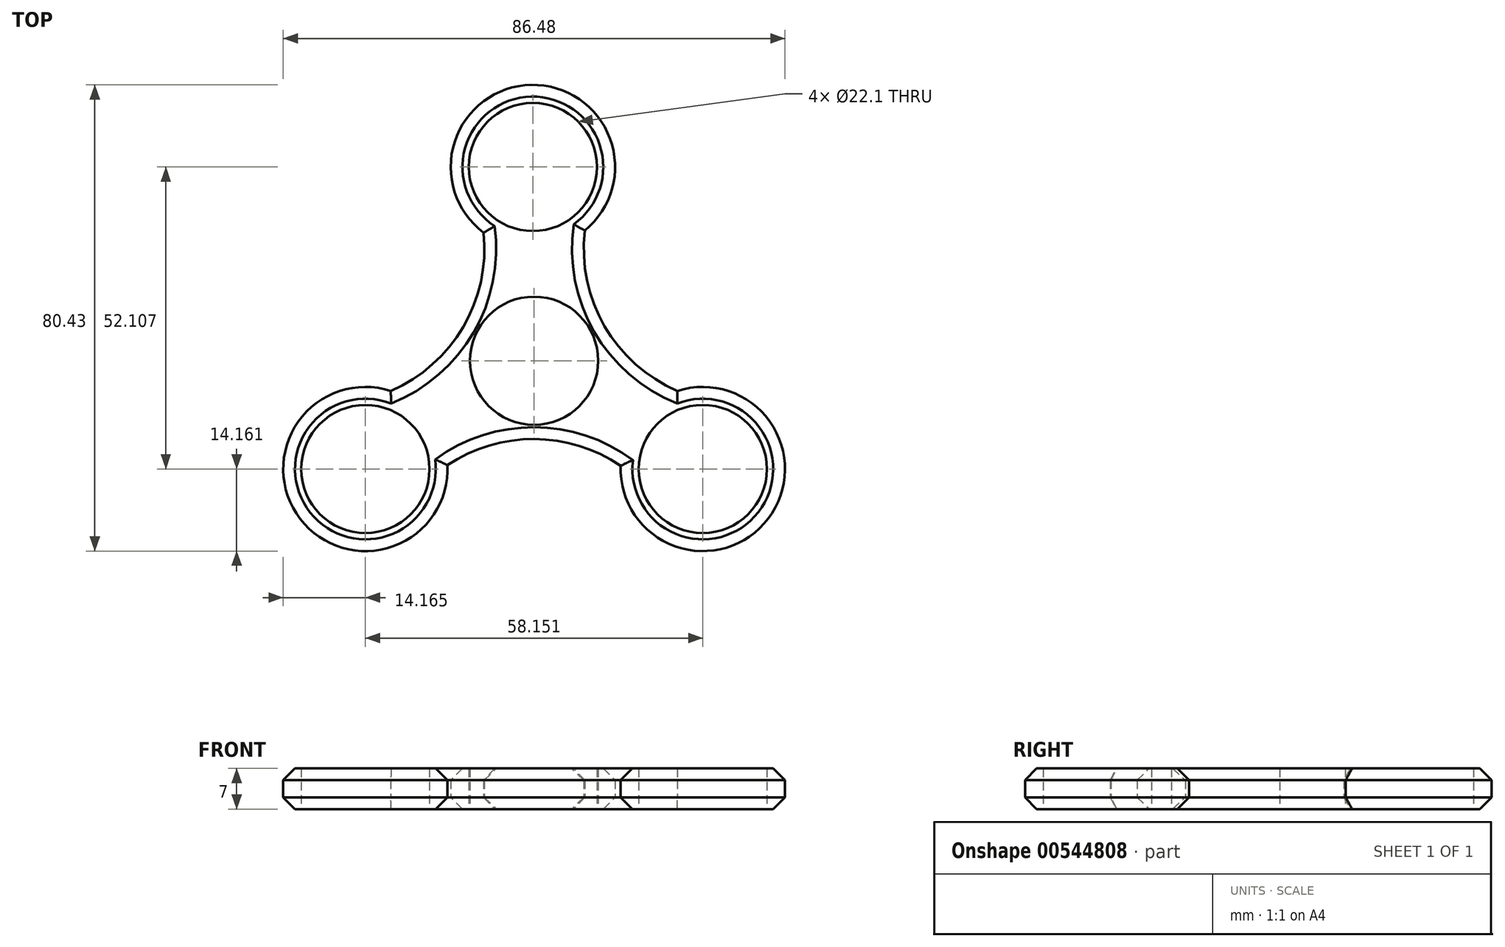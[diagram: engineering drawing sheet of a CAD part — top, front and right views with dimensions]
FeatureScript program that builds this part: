
annotation { "Feature Type Name" : "Feature", "Feature Type Description" : "" }
export const myFeature = defineFeature(function(context is Context, id is Id, definition is map)
    precondition{}
    {
        {
            var Q0;
            Q0=qCreatedBy(makeId("Top.planeOp"),FACE);
            var sketch = newSketch(context, id + "F0", { "sketchPlane" : qUnion([Q0])});
            skCircle(sketch, "E0", {"center": v(0, 0) * mm, "radius": 11.05 * mm});
            skLineSegment(sketch, "E1", {"start": v(0, 0) * mm, "end": v(0, 33.02) * mm, "construction": true});
            skLineSegment(sketch, "E2", {"start": v(0, 0) * mm, "end": v(-28.27, -17.07) * mm, "construction": true});
            skCircle(sketch, "E3", {"center": v(-29.08, -18.68) * mm, "radius": 11.05 * mm});
            skCircle(sketch, "E4.MirrorC", {"center": v(29.08, -18.68) * mm, "radius": 11.05 * mm});
            skLineSegment(sketch, "E5.MirrorCS", {"start": v(0, 0) * mm, "end": v(28.27, -17.07) * mm, "construction": true});
            skLineSegment(sketch, "E6", {"start": v(-8.81, 22.99) * mm, "end": v(-25.05, -5.78) * mm, "construction": true});
            skArc(sketch, "E7", {"start": v(-24.9, -5.29) * mm, "mid": v(-12.06, 6.12) * mm, "end": v(-8.81, 22.99) * mm});
            skArc(sketch, "E8.MirrorCS", {"start": v(24.9, -5.29) * mm, "mid": v(12.06, 6.12) * mm, "end": v(8.81, 22.99) * mm});
            skLineSegment(sketch, "E9", {"start": v(8.81, 22.99) * mm, "end": v(8.95, 23.98) * mm});
            skLineSegment(sketch, "E10", {"start": v(-15.56, -18.68) * mm, "end": v(15.56, -18.68) * mm, "construction": true});
            skArc(sketch, "E11", {"start": v(15.7, -18.68) * mm, "mid": v(-0.08, -13.51) * mm, "end": v(-15.88, -18.68) * mm});
            skCircle(sketch, "E12", {"center": v(-0.21, 33.43) * mm, "radius": 11.05 * mm});
            skLineSegment(sketch, "E13", {"start": v(-8.81, 22.99) * mm, "end": v(-8.82, 23.02) * mm});
            skLineSegment(sketch, "E14", {"start": v(-9.53, 5.6) * mm, "end": v(12.37, 5.6) * mm, "construction": true});
            skLineSegment(sketch, "E15", {"start": v(-24.9, -5.29) * mm, "end": v(-25.65, -5.6) * mm});
            skLineSegment(sketch, "E16", {"start": v(24.9, -5.29) * mm, "end": v(25.65, -5.6) * mm});
            skCircle(sketch, "E17", {"center": v(-0.21, 33.43) * mm, "radius": 14.16 * mm});
            skCircle(sketch, "E18", {"center": v(29.08, -18.68) * mm, "radius": 14.16 * mm});
            skCircle(sketch, "E19", {"center": v(-29.08, -18.68) * mm, "radius": 14.16 * mm});
            skLineSegment(sketch, "E20", {"start": v(-29.08, -18.68) * mm, "end": v(-29.08, -36.84) * mm, "construction": true});
            skLineSegment(sketch, "E21", {"start": v(-29.08, -36.84) * mm, "end": v(-29.08, -32.84) * mm, "construction": true});
            skLineSegment(sketch, "E22", {"start": v(-29.08, -32.84) * mm, "end": v(37.92, -32.84) * mm, "construction": true});
            skLineSegment(sketch, "E23", {"start": v(37.92, -32.84) * mm, "end": v(29.08, -32.84) * mm, "construction": true});
            skLineSegment(sketch, "E24", {"start": v(29.08, -32.84) * mm, "end": v(29.08, 34.26) * mm, "construction": true});
            skSolve(sketch);
        }
        {
            var Q0;
            Q0 = qSketchRegion(id + "F0", true);
            extrude(context, id + "F1", {"entities" : qUnion([Q0]), "depth" : 7 * mm, "offsetDistance" : 25.4 * mm});
        }
        {
            var Q0;
            Q0=makeQuery(id+"F1.opExtrude","CAP_EDGE",EDGE,{"disambiguationData":[OSD([sQuery(id+"F0.wireOp",EDGE,"E7")])],"isStart":false});
            var Q1;
            Q1=makeQuery(id+"F1.opExtrude","CAP_EDGE",EDGE,{"disambiguationData":[OSD([sQuery(id+"F0.wireOp",EDGE,"E8.MirrorCS")])],"isStart":false});
            var Q2;
            Q2=makeQuery(id+"F1.opExtrude","CAP_EDGE",EDGE,{"disambiguationData":[OSD([sQuery(id+"F0.wireOp",EDGE,"E11")])],"isStart":false});
            var Q3;
            Q3=makeQuery(id+"F1.opExtrude","CAP_EDGE",EDGE,{"disambiguationData":[OSD([sQuery(id+"F0.wireOp",EDGE,"E11")])],"isStart":true});
            var Q4;
            Q4=makeQuery(id+"F1.opExtrude","CAP_EDGE",EDGE,{"disambiguationData":[OSD([sQuery(id+"F0.wireOp",EDGE,"E8.MirrorCS")])],"isStart":true});
            var Q5;
            Q5=makeQuery(id+"F1.opExtrude","CAP_EDGE",EDGE,{"disambiguationData":[OSD([sQuery(id+"F0.wireOp",EDGE,"E7")])],"isStart":true});
            var Q6;
            Q6=makeQuery(id+"F1.opExtrude","CAP_EDGE",EDGE,{"disambiguationData":[OSD([sQuery(id+"F0.wireOp",EDGE,"80e09b6a-21da-49b2-8cf5-6d680d49bf07")])],"isStart":true});
            var Q7;
            Q7=makeQuery(id+"F1.opExtrude","CAP_EDGE",EDGE,{"disambiguationData":[OSD([sQuery(id+"F0.wireOp",EDGE,"16e0cbf3-41ad-4127-a740-f7c4efafd8980.MirrorC")])],"isStart":true});
            var Q8;
            Q8=makeQuery(id+"F1.opExtrude","CAP_EDGE",EDGE,{"disambiguationData":[OSD([sQuery(id+"F0.wireOp",EDGE,"676988b3-80e1-4ee0-a835-973b64eb649f")])],"isStart":true});
            var Q9;
            Q9=makeQuery(id+"F1.opExtrude","CAP_EDGE",EDGE,{"disambiguationData":[OSD([sQuery(id+"F0.wireOp",EDGE,"676988b3-80e1-4ee0-a835-973b64eb649f")])],"isStart":false});
            var Q10;
            Q10=makeQuery(id+"F1.opExtrude","CAP_EDGE",EDGE,{"disambiguationData":[OSD([sQuery(id+"F0.wireOp",EDGE,"16e0cbf3-41ad-4127-a740-f7c4efafd8980.MirrorC")])],"isStart":false});
            var Q11;
            Q11=makeQuery(id+"F1.opExtrude","CAP_EDGE",EDGE,{"disambiguationData":[OSD([sQuery(id+"F0.wireOp",EDGE,"80e09b6a-21da-49b2-8cf5-6d680d49bf07")])],"isStart":false});
            var Q12;
            Q12=makeQuery(id+"F1.opExtrude","CAP_EDGE",EDGE,{"disambiguationData":[OSD([sQuery(id+"F0.wireOp",EDGE,"E19")])],"isStart":true});
            var Q13;
            Q13=makeQuery(id+"F1.opExtrude","CAP_EDGE",EDGE,{"disambiguationData":[OSD([sQuery(id+"F0.wireOp",EDGE,"E18")])],"isStart":true});
            var Q14;
            Q14=makeQuery(id+"F1.opExtrude","CAP_EDGE",EDGE,{"disambiguationData":[OSD([sQuery(id+"F0.wireOp",EDGE,"E17")])],"isStart":true});
            var Q15;
            Q15=makeQuery(id+"F1.opExtrude","CAP_EDGE",EDGE,{"disambiguationData":[OSD([sQuery(id+"F0.wireOp",EDGE,"E19")])],"isStart":false});
            var Q16;
            Q16=makeQuery(id+"F1.opExtrude","CAP_EDGE",EDGE,{"disambiguationData":[OSD([sQuery(id+"F0.wireOp",EDGE,"E18")])],"isStart":false});
            var Q17;
            Q17=makeQuery(id+"F1.opExtrude","CAP_EDGE",EDGE,{"disambiguationData":[OSD([sQuery(id+"F0.wireOp",EDGE,"E17")])],"isStart":false});
            chamfer(context, id + "F2", {"entities" : qUnion([Q0, Q1, Q2, Q3, Q4, Q5, Q6, Q7, Q8, Q9, Q10, Q11, Q12, Q13, Q14, Q15, Q16, Q17]), "width" : 2.03 * mm, "tangentPropagation" : true});
        }
    });
